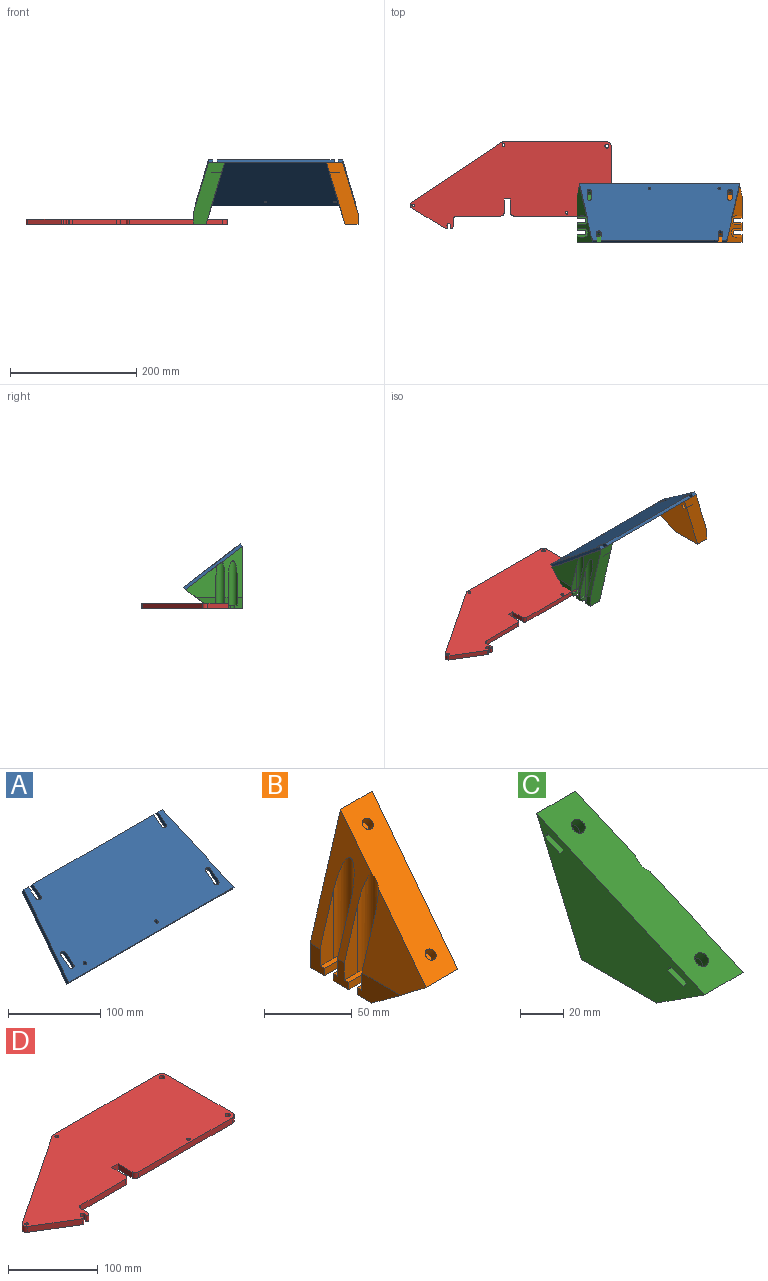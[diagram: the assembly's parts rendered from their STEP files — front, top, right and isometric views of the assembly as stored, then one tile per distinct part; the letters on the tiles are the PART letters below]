
ASSEMBLY  parts=4 mates=5
PART A: 24 faces, bbox 253.7x92.6x72.9 mm
  f0: cylinder r=3.5mm len=7mm, axis (0,0.61,-0.79), area 55mm2, adj f1,f21,f22,f23
  f1: plane 14.94x13.11mm, normal (1,0,0), area 75mm2, adj f0,f2,f22,f23
  f2: cylinder r=3.5mm len=7mm, axis (0,0.61,-0.79), area 55mm2, adj f1,f21,f22,f23
  f3: plane 14.94x13.11mm, normal (1,0,0), area 75mm2, adj f4,f19,f22,f23
  f4: cylinder r=3.5mm len=7mm, axis (0,0.61,-0.79), area 55mm2, adj f3,f5,f22,f23
  f5: plane 14.94x13.11mm, normal (-1,0,0), area 75mm2, adj f4,f19,f22,f23
  f6: plane 92.62x72.86mm, normal (-0.98,0.14,0.11), area 574.5mm2, adj f7,f20,f22,f23
  f7: plane 253.7x3.96mm, normal (0,-0.79,-0.61), area 1268.5mm2, adj f6,f8,f22,f23
  f8: plane 92.62x72.86mm, normal (0.98,0.14,0.11), area 574.5mm2, adj f7,f9,f22,f23
  f9: plane 6.54x3.96mm, normal (0,0.79,0.61), area 32.7mm2, adj f8,f10,f22,f23
  f10: plane 14.94x13.11mm, normal (-1,0,0), area 75mm2, adj f9,f11,f22,f23
  f11: cylinder r=3.5mm len=7mm, axis (0,0.61,-0.79), area 55mm2, adj f10,f12,f22,f23
  f12: plane 14.94x13.11mm, normal (1,0,0), area 75mm2, adj f11,f13,f22,f23
  f13: plane 185.1x3.96mm, normal (0,0.79,0.61), area 925.5mm2, adj f12,f14,f22,f23
  f14: plane 14.94x13.11mm, normal (-1,0,0), area 75mm2, adj f13,f15,f22,f23
  f15: cylinder r=3.5mm len=7mm, axis (0,0.61,-0.79), area 55mm2, adj f14,f16,f22,f23
  f16: plane 14.94x13.11mm, normal (1,0,0), area 75mm2, adj f15,f20,f22,f23
  f17: cylinder r=2mm len=6.4mm, axis (0,0.61,-0.79), area 62.8mm2, adj f22,f23
  f18: cylinder r=2mm len=6.4mm, axis (0,0.61,-0.79), area 62.8mm2, adj f22,f23
  f19: cylinder r=3.5mm len=7mm, axis (0,0.61,-0.79), area 55mm2, adj f3,f5,f22,f23
  f20: plane 6.54x3.96mm, normal (0,0.79,0.61), area 32.7mm2, adj f6,f16,f22,f23
  f21: plane 14.94x13.11mm, normal (-1,0,0), area 75mm2, adj f0,f2,f22,f23
  f22: plane 253.7x89.57mm, normal (0,-0.61,0.79), area 25761.4mm2, adj f0,f1,f2,f3,f4,f5,f6,f7
  f23: plane 253.7x89.57mm, normal (0,0.61,-0.79), area 25761.4mm2, adj f0,f1,f2,f3,f4,f5,f6,f7
PART B: 40 faces, bbox 50x89.6x97.9 mm
  f0: plane 49.57x20.5mm, normal (0,0,-1), area 830.6mm2, adj f2,f3,f4,f5,f6,f7,f14,f15
  f1: plane 89.57x68.9mm, normal (0,-0.61,0.79), area 2805.9mm2, adj f4,f5,f6,f12,f22,f23,f24,f25
  f2: plane 16.89x12.57mm, normal (-1,0,0), area 129mm2, adj f0,f8,f13,f14,f17,f20,f21,f22
  f3: plane 16.89x11.5mm, normal (-1,0,0), area 152.6mm2, adj f0,f4,f10,f18,f21,f22
  f4: plane 97.9x50mm, normal (0,1,0), area 2462.1mm2, adj f0,f1,f3,f6,f22
  f5: plane 40x29.24mm, normal (0,-0.59,-0.81), area 1191mm2, adj f0,f1,f6,f7,f23
  f6: plane 97.9x89.57mm, normal (0.96,0,-0.29), area 5197.9mm2, adj f0,f1,f4,f5,f26,f28,f29,f30
  f7: plane 34.79x16.89mm, normal (-1,0,0), area 349.2mm2, adj f0,f5,f11,f16,f17,f23
  f8: plane 46.73x10.5mm, normal (0,1,0), area 307.7mm2, adj f2,f9,f21,f22
  f9: cylinder r=7mm len=70.04mm, axis (0,0,-1), area 1352.9mm2, adj f8,f10,f21,f22
  f10: plane 46.73x10.5mm, normal (0,-1,0), area 307.7mm2, adj f3,f9,f21,f22
  f11: plane 46.73x10.5mm, normal (0,1,0), area 307.7mm2, adj f7,f12,f17,f23
  f12: cylinder r=7mm len=68.3mm, axis (0,0,-1), area 1328.8mm2, adj f1,f11,f13,f17,f22,f23
  f13: plane 46.73x10.5mm, normal (0,-1,0), area 307.7mm2, adj f2,f12,f17,f22
  f14: plane 10.5x5mm, normal (0,-1,0), area 52.5mm2, adj f0,f2,f15,f17
  f15: cylinder r=3.5mm len=7mm, axis (0,0,-1), area 55mm2, adj f0,f14,f16,f17
  f16: plane 10.5x5mm, normal (0,1,0), area 52.5mm2, adj f0,f7,f15,f17
  f17: plane 17.5x14mm, normal (0,0,1), area 131.2mm2, adj f2,f7,f11,f12,f13,f14,f15,f16
  f18: plane 10.5x5mm, normal (0,-1,0), area 52.5mm2, adj f0,f3,f19,f21
  f19: cylinder r=3.5mm len=7mm, axis (0,0,-1), area 55mm2, adj f0,f18,f20,f21
  f20: plane 10.5x5mm, normal (0,1,0), area 52.5mm2, adj f0,f2,f19,f21
  f21: plane 17.5x14mm, normal (0,0,1), area 131.2mm2, adj f2,f3,f8,f9,f10,f18,f19,f20
  f22: plane 81.01x31.97mm, normal (-0.96,0,0.29), area 1286mm2, adj f1,f2,f3,f4,f8,f9,f10,f12
  f23: plane 50.43x49.81mm, normal (-0.96,0,0.29), area 1435.1mm2, adj f1,f5,f7,f11,f12
  f24: cylinder r=3.5mm len=9.21mm, axis (0,-0.61,0.79), area 131.9mm2, adj f1,f34
  f25: cylinder r=3.5mm len=9.21mm, axis (0,-0.61,0.79), area 131.9mm2, adj f1,f29
  f26: plane 15.65x4.76mm, normal (0,0.79,0.61), area 89.6mm2, adj f6,f27,f29,f30
  f27: plane 11.98x11.16mm, normal (1,0,0), area 63mm2, adj f26,f28,f29,f30
  f28: plane 17.58x4.76mm, normal (0,-0.79,-0.61), area 101.2mm2, adj f6,f27,f29,f30
  f29: plane 17.58x8.32mm, normal (0,0.61,-0.79), area 135.9mm2, adj f6,f25,f26,f27,f28
  f30: plane 16.14x8.32mm, normal (0,-0.61,0.79), area 120.9mm2, adj f6,f26,f27,f28,f37
  f31: plane 15.65x4.76mm, normal (0,0.79,0.61), area 89.6mm2, adj f6,f32,f34,f35
  f32: plane 11.98x11.16mm, normal (1,0,0), area 63mm2, adj f31,f33,f34,f35
  f33: plane 17.58x4.76mm, normal (0,-0.79,-0.61), area 101.2mm2, adj f6,f32,f34,f35
  f34: plane 17.58x8.32mm, normal (0,0.61,-0.79), area 135.9mm2, adj f6,f24,f31,f32,f33
  f35: plane 16.14x8.32mm, normal (0,-0.61,0.79), area 120.9mm2, adj f6,f31,f32,f33,f39
  f36: plane 7x5.55mm, normal (0,-0.61,0.79), area 38.5mm2, adj f37
  f37: cylinder r=3.5mm len=7mm, axis (0,-0.61,0.79), area 22mm2, adj f30,f36
  f38: plane 7x5.55mm, normal (0,-0.61,0.79), area 38.5mm2, adj f39
  f39: cylinder r=3.5mm len=7mm, axis (0,-0.61,0.79), area 22mm2, adj f35,f38
PART C: 40 faces, bbox 50x89.6x97.9 mm
  f0: plane 49.57x20.5mm, normal (0,0,-1), area 830.6mm2, adj f2,f3,f4,f5,f6,f7,f14,f15
  f1: plane 89.57x68.9mm, normal (0,-0.61,0.79), area 2805.9mm2, adj f4,f5,f6,f12,f22,f23,f24,f25
  f2: plane 16.89x12.57mm, normal (1,0,0), area 129mm2, adj f0,f8,f13,f14,f17,f20,f21,f22
  f3: plane 16.89x11.5mm, normal (1,0,0), area 152.6mm2, adj f0,f4,f10,f18,f21,f22
  f4: plane 97.9x50mm, normal (0,1,0), area 2462.1mm2, adj f0,f1,f3,f6,f22
  f5: plane 40x29.24mm, normal (0,-0.59,-0.81), area 1191mm2, adj f0,f1,f6,f7,f23
  f6: plane 97.9x89.57mm, normal (-0.96,0,-0.29), area 5197.9mm2, adj f0,f1,f4,f5,f26,f28,f29,f30
  f7: plane 34.79x16.89mm, normal (1,0,0), area 349.2mm2, adj f0,f5,f11,f16,f17,f23
  f8: plane 46.73x10.5mm, normal (0,1,0), area 307.7mm2, adj f2,f9,f21,f22
  f9: cylinder r=7mm len=70.04mm, axis (0,0,-1), area 1352.9mm2, adj f8,f10,f21,f22
  f10: plane 46.73x10.5mm, normal (0,-1,0), area 307.7mm2, adj f3,f9,f21,f22
  f11: plane 46.73x10.5mm, normal (0,1,0), area 307.7mm2, adj f7,f12,f17,f23
  f12: cylinder r=7mm len=68.3mm, axis (0,0,-1), area 1328.8mm2, adj f1,f11,f13,f17,f22,f23
  f13: plane 46.73x10.5mm, normal (0,-1,0), area 307.7mm2, adj f2,f12,f17,f22
  f14: plane 10.5x5mm, normal (0,-1,0), area 52.5mm2, adj f0,f2,f15,f17
  f15: cylinder r=3.5mm len=7mm, axis (0,0,-1), area 55mm2, adj f0,f14,f16,f17
  f16: plane 10.5x5mm, normal (0,1,0), area 52.5mm2, adj f0,f7,f15,f17
  f17: plane 17.5x14mm, normal (0,0,1), area 131.2mm2, adj f2,f7,f11,f12,f13,f14,f15,f16
  f18: plane 10.5x5mm, normal (0,-1,0), area 52.5mm2, adj f0,f3,f19,f21
  f19: cylinder r=3.5mm len=7mm, axis (0,0,-1), area 55mm2, adj f0,f18,f20,f21
  f20: plane 10.5x5mm, normal (0,1,0), area 52.5mm2, adj f0,f2,f19,f21
  f21: plane 17.5x14mm, normal (0,0,1), area 131.2mm2, adj f2,f3,f8,f9,f10,f18,f19,f20
  f22: plane 81.01x31.97mm, normal (0.96,0,0.29), area 1286mm2, adj f1,f2,f3,f4,f8,f9,f10,f12
  f23: plane 50.43x49.81mm, normal (0.96,0,0.29), area 1435.1mm2, adj f1,f5,f7,f11,f12
  f24: cylinder r=3.5mm len=9.21mm, axis (0,-0.61,0.79), area 131.9mm2, adj f1,f34
  f25: cylinder r=3.5mm len=9.21mm, axis (0,-0.61,0.79), area 131.9mm2, adj f1,f29
  f26: plane 15.65x4.76mm, normal (0,0.79,0.61), area 89.6mm2, adj f6,f27,f29,f30
  f27: plane 11.98x11.16mm, normal (-1,0,0), area 63mm2, adj f26,f28,f29,f30
  f28: plane 17.58x4.76mm, normal (0,-0.79,-0.61), area 101.2mm2, adj f6,f27,f29,f30
  f29: plane 17.58x8.32mm, normal (0,0.61,-0.79), area 135.9mm2, adj f6,f25,f26,f27,f28
  f30: plane 16.14x8.32mm, normal (0,-0.61,0.79), area 120.9mm2, adj f6,f26,f27,f28,f37
  f31: plane 15.65x4.76mm, normal (0,0.79,0.61), area 89.6mm2, adj f6,f32,f34,f35
  f32: plane 11.98x11.16mm, normal (-1,0,0), area 63mm2, adj f31,f33,f34,f35
  f33: plane 17.58x4.76mm, normal (0,-0.79,-0.61), area 101.2mm2, adj f6,f32,f34,f35
  f34: plane 17.58x8.32mm, normal (0,0.61,-0.79), area 135.9mm2, adj f6,f24,f31,f32,f33
  f35: plane 16.14x8.32mm, normal (0,-0.61,0.79), area 120.9mm2, adj f6,f31,f32,f33,f39
  f36: plane 7x5.55mm, normal (0,-0.61,0.79), area 38.5mm2, adj f37
  f37: cylinder r=3.5mm len=7mm, axis (0,-0.61,0.79), area 22mm2, adj f30,f36
  f38: plane 7x5.55mm, normal (0,-0.61,0.79), area 38.5mm2, adj f39
  f39: cylinder r=3.5mm len=7mm, axis (0,-0.61,0.79), area 22mm2, adj f35,f38
PART D: 30 faces, bbox 318.5x137.7x8 mm
  f0: cylinder r=3mm len=8mm, axis (0,0,-1), area 104.8mm2, adj f22,f23,f27,f29
  f1: cylinder r=7mm len=8mm, axis (0,0,-1), area 34.3mm2, adj f2,f22,f23,f27
  f2: plane 10x8mm, normal (1,0,0), area 80mm2, adj f1,f22,f23,f24
  f3: plane 70.5x8mm, normal (0,-1,0), area 564mm2, adj f22,f23,f24,f25
  f4: plane 22x8mm, normal (1,0,0), area 176mm2, adj f5,f22,f23,f25
  f5: plane 10x8mm, normal (0,-1,0), area 80mm2, adj f4,f6,f22,f23
  f6: plane 22x8mm, normal (-1,0,0), area 176mm2, adj f5,f22,f23,f26
  f7: plane 147.5x8mm, normal (0,-1,0), area 1180mm2, adj f8,f22,f23,f26
  f8: cylinder r=7mm len=8mm, axis (0,0,-1), area 88mm2, adj f7,f9,f22,f23
  f9: plane 103.5x8mm, normal (1,0,0), area 828mm2, adj f8,f10,f22,f23
  f10: cylinder r=7mm len=8mm, axis (0,0,-1), area 88mm2, adj f9,f11,f22,f23
  f11: plane 163.5x8mm, normal (0,1,0), area 1308mm2, adj f10,f12,f22,f23
  f12: cylinder r=5mm len=8mm, axis (0,0,-1), area 23.6mm2, adj f11,f13,f22,f23
  f13: plane 143x95.5mm, normal (-0.56,0.83,0), area 1375.7mm2, adj f12,f14,f22,f23
  f14: cylinder r=5mm len=8.43mm, axis (0,0,-1), area 80.3mm2, adj f13,f15,f22,f23
  f15: plane 53.75x32.67mm, normal (-0.52,-0.85,0), area 503.2mm2, adj f14,f22,f23,f28
  f16: cylinder r=3mm len=8mm, axis (0,0,-1), area 150.8mm2, adj f22,f23
  f17: cylinder r=3mm len=8mm, axis (0,0,-1), area 150.8mm2, adj f22,f23
  f18: cylinder r=2mm len=8mm, axis (0,0,-1), area 100.5mm2, adj f22,f23
  f19: cylinder r=2mm len=8mm, axis (0,0,-1), area 100.5mm2, adj f22,f23
  f20: cylinder r=2mm len=8mm, axis (0,0,-1), area 100.5mm2, adj f22,f23
  f21: plane 8x0.36mm, normal (0.85,-0.52,0), area 3.3mm2, adj f22,f23,f28,f29
  f22: plane 318.5x137.73mm, normal (0,0,1), area 30231mm2, adj f0,f1,f2,f3,f4,f5,f6,f7
  f23: plane 318.5x137.73mm, normal (0,0,-1), area 30231mm2, adj f0,f1,f2,f3,f4,f5,f6,f7
  f24: cylinder r=5mm len=8mm, axis (0,0,-1), area 62.8mm2, adj f2,f3,f22,f23
  f25: cylinder r=5mm len=8mm, axis (0,0,-1), area 62.8mm2, adj f3,f4,f22,f23
  f26: cylinder r=5mm len=8mm, axis (0,0,1), area 62.8mm2, adj f6,f7,f22,f23
  f27: cylinder r=2mm len=8mm, axis (0,0,-1), area 50.3mm2, adj f0,f1,f22,f23
  f28: cylinder r=2mm len=8mm, axis (0,0,1), area 25.1mm2, adj f15,f21,f22,f23
  f29: cylinder r=2mm len=8mm, axis (0,0,-1), area 18.5mm2, adj f0,f21,f22,f23
PLACE A rot(axis=(0,0,-1),180deg) t=(241.1,-133.48,-3.38)mm
PLACE B rot(axis=(0,0,-1),180deg) t=(241.1,-133.48,-3.38)mm
PLACE C rot(axis=(0,0,-1),180deg) t=(241.1,-133.48,-3.38)mm
PLACE D t=(32.54,60.48,-3.38)mm fixed
MATE revolute A.f0 <-> B.f25  axis (0,-0.61,-0.79) through (352.4,-15.84,34.76)mm
MATE revolute C.f24 <-> A.f11  axis (0,0.61,0.79) through (145.05,-81.63,85.37)mm
MATE planar C.f0 <-> D.f23  axis (0,0,-1) through (120.85,-43.95,-3.38)mm
MATE revolute A.f15 <-> B.f24  axis (0,-0.61,-0.79) through (337.15,-81.63,85.37)mm
MATE revolute C.f25 <-> A.f19  axis (0,0.61,0.79) through (129.8,-15.84,34.76)mm
